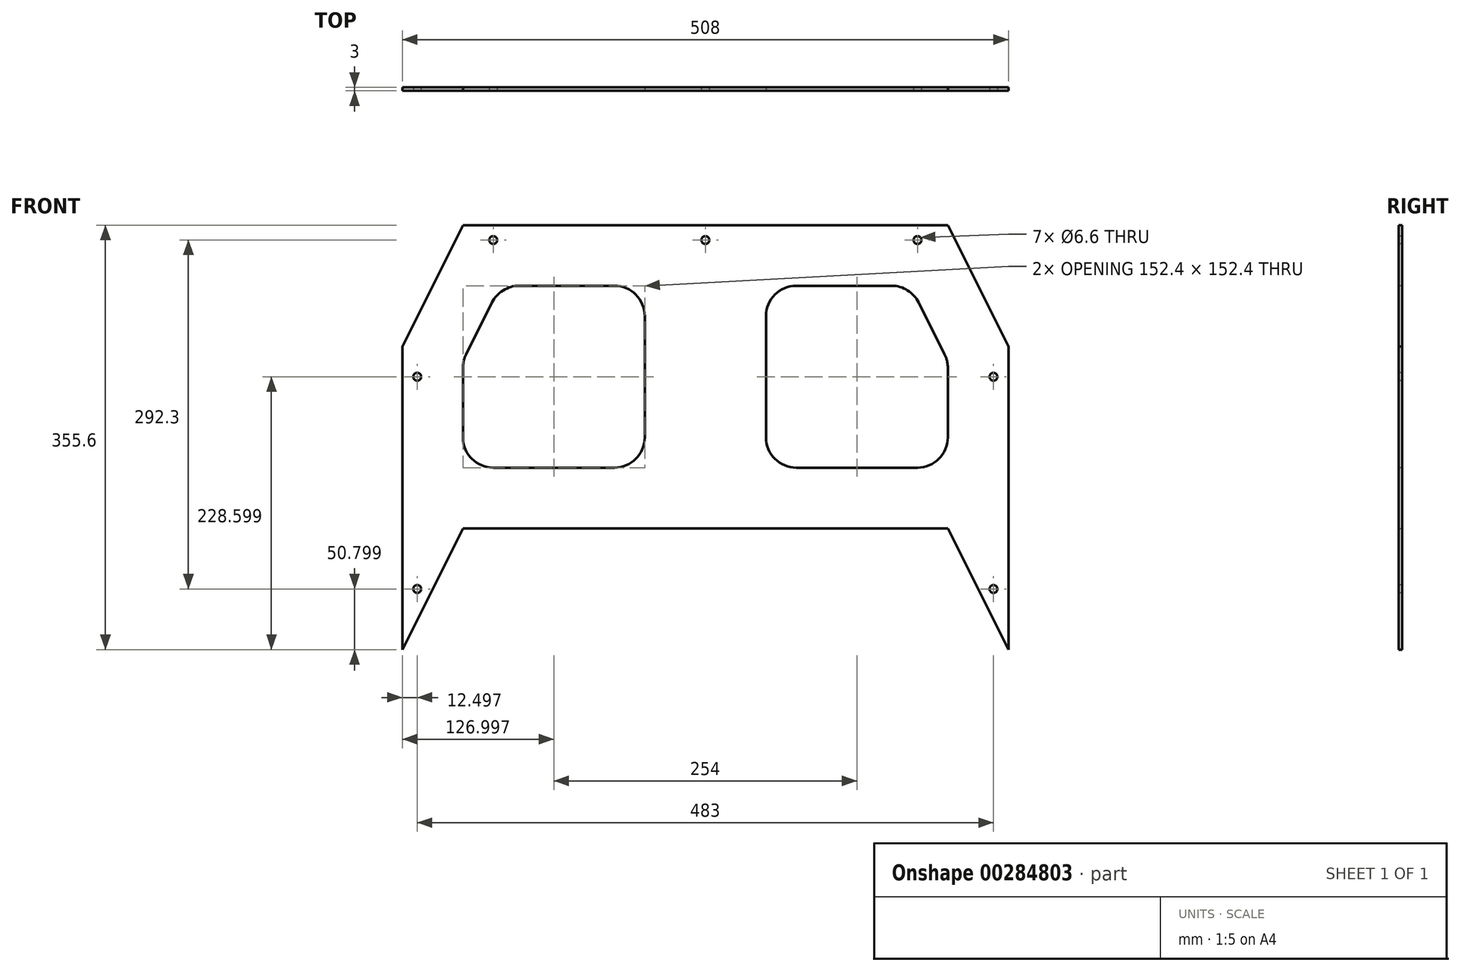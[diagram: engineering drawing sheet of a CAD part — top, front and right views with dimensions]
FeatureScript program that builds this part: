
annotation { "Feature Type Name" : "Feature", "Feature Type Description" : "" }
export const myFeature = defineFeature(function(context is Context, id is Id, definition is map)
    precondition{}
    {
        {
            var Q0;
            Q0=qCreatedBy(makeId("Front.planeOp"),FACE);
            var sketch = newSketch(context, id + "F0", { "sketchPlane" : qUnion([Q0])});
            skLineSegment(sketch, "E0", {"start": v(-249.2, -132.6) * mm, "end": v(-249.2, 121.4) * mm});
            skLineSegment(sketch, "E1", {"start": v(-249.2, 121.4) * mm, "end": v(-198.4, 223) * mm});
            skLineSegment(sketch, "E2", {"start": v(-198.4, 223) * mm, "end": v(208, 223) * mm});
            skLineSegment(sketch, "E3", {"start": v(208, 223) * mm, "end": v(258.8, 121.4) * mm});
            skLineSegment(sketch, "E4", {"start": v(258.8, 121.4) * mm, "end": v(258.8, -132.6) * mm});
            skLineSegment(sketch, "E5", {"start": v(-249.2, -132.6) * mm, "end": v(-198.4, -31) * mm});
            skLineSegment(sketch, "E6", {"start": v(-198.4, -31) * mm, "end": v(208, -31) * mm});
            skLineSegment(sketch, "E7", {"start": v(208, -31) * mm, "end": v(258.8, -132.6) * mm});
            skSolve(sketch);
        }
        {
            var Q0;
            Q0 = qSketchRegion(id + "F0", true);
            extrude(context, id + "F1", {"entities" : qUnion([Q0]), "depth" : 3 * mm});
        }
        {
            var Q0;
            Q0=makeQuery(id+"F1.opExtrude","CAP_FACE",FACE,{"disambiguationData":[OSD([sQuery(id+"F0.wireOp",EDGE,"E0"),sQuery(id+"F0.wireOp",EDGE,"E1"),sQuery(id+"F0.wireOp",EDGE,"E2"),sQuery(id+"F0.wireOp",EDGE,"E3"),sQuery(id+"F0.wireOp",EDGE,"E4"),sQuery(id+"F0.wireOp",EDGE,"E5"),sQuery(id+"F0.wireOp",EDGE,"E6"),sQuery(id+"F0.wireOp",EDGE,"E7")])],"isStart":false});
            var sketch = newSketch(context, id + "F2", { "sketchPlane" : qUnion([Q0])});
            skLineSegment(sketch, "E8", {"start": v(-173, 19.8) * mm, "end": v(-71.4, 19.8) * mm});
            skLineSegment(sketch, "E9", {"start": v(-46, 45.2) * mm, "end": v(-46, 146.8) * mm});
            skLineSegment(sketch, "E10", {"start": v(-71.4, 172.2) * mm, "end": v(-151.3, 172.2) * mm});
            skLineSegment(sketch, "E11", {"start": v(-174.02, 158.17) * mm, "end": v(-195.71, 114.78) * mm});
            skLineSegment(sketch, "E12", {"start": v(-198.4, 103.42) * mm, "end": v(-198.4, 45.2) * mm});
            skPoint(sketch, "E13.visualSharp", {"position": v(-167, 172.2) * mm});
            skArc(sketch, "E13.filletArc", {"start": v(-151.3, 172.2) * mm, "mid": v(-164.65, 168.42) * mm, "end": v(-174.02, 158.17) * mm});
            skPoint(sketch, "E14.visualSharp", {"position": v(-46, 172.2) * mm});
            skArc(sketch, "E14.filletArc", {"start": v(-46, 146.8) * mm, "mid": v(-53.43, 164.77) * mm, "end": v(-71.4, 172.2) * mm});
            skPoint(sketch, "E15.visualSharp", {"position": v(-46, 19.8) * mm});
            skArc(sketch, "E15.filletArc", {"start": v(-71.4, 19.8) * mm, "mid": v(-53.43, 27.25) * mm, "end": v(-46, 45.2) * mm});
            skPoint(sketch, "E16.visualSharp", {"position": v(-198.4, 19.8) * mm});
            skArc(sketch, "E16.filletArc", {"start": v(-198.4, 45.2) * mm, "mid": v(-190.95, 27.25) * mm, "end": v(-173, 19.8) * mm});
            skPoint(sketch, "E17.visualSharp", {"position": v(-198.4, 109.42) * mm});
            skArc(sketch, "E17.filletArc", {"start": v(-195.71, 114.78) * mm, "mid": v(-197.71, 109.26) * mm, "end": v(-198.4, 103.42) * mm});
            skArc(sketch, "E18.MirrorCS", {"start": v(205.33, 114.78) * mm, "mid": v(207.33, 109.26) * mm, "end": v(208, 103.42) * mm});
            skArc(sketch, "E19.MirrorCS", {"start": v(160.91, 172.2) * mm, "mid": v(174.27, 168.42) * mm, "end": v(183.63, 158.17) * mm});
            skLineSegment(sketch, "E20.MirrorCS", {"start": v(81, 172.2) * mm, "end": v(160.91, 172.2) * mm});
            skLineSegment(sketch, "E21.MirrorCS", {"start": v(55.6, 45.2) * mm, "end": v(55.6, 146.8) * mm});
            skLineSegment(sketch, "E22.MirrorCS", {"start": v(182.6, 19.8) * mm, "end": v(81, 19.8) * mm});
            skArc(sketch, "E23.MirrorCS", {"start": v(55.6, 146.8) * mm, "mid": v(63.05, 164.77) * mm, "end": v(81, 172.2) * mm});
            skPoint(sketch, "E24.MirrorP", {"position": v(176.61, 172.2) * mm});
            skArc(sketch, "E25.MirrorCS", {"start": v(81, 19.8) * mm, "mid": v(63.05, 27.25) * mm, "end": v(55.6, 45.2) * mm});
            skLineSegment(sketch, "E26.MirrorCS", {"start": v(183.63, 158.17) * mm, "end": v(205.33, 114.78) * mm});
            skPoint(sketch, "E27.MirrorP", {"position": v(55.6, 172.2) * mm});
            skPoint(sketch, "E28.MirrorP", {"position": v(208, 19.8) * mm});
            skPoint(sketch, "E29.MirrorP", {"position": v(55.6, 19.8) * mm});
            skArc(sketch, "E30.MirrorCS", {"start": v(208, 45.2) * mm, "mid": v(200.57, 27.25) * mm, "end": v(182.6, 19.8) * mm});
            skPoint(sketch, "E31.MirrorP", {"position": v(208, 109.42) * mm});
            skLineSegment(sketch, "E32.MirrorCS", {"start": v(208, 103.42) * mm, "end": v(208, 45.2) * mm});
            skSolve(sketch);
        }
        {
            var Q0;
            Q0 = qSketchRegion(id + "F2", true);
            extrude(context, id + "F3", {"entities" : qUnion([Q0]), "operationType" : NewBodyOperationType.REMOVE, "endBound" : BoundingType.THROUGH_ALL, "oppositeDirection" : true, "depth" : 25 * mm});
        }
        {
            var Q0;
            Q0=makeQuery(id+"F1.opExtrude","CAP_FACE",FACE,{"disambiguationData":[OSD([sQuery(id+"F0.wireOp",EDGE,"E0"),sQuery(id+"F0.wireOp",EDGE,"E1"),sQuery(id+"F0.wireOp",EDGE,"E2"),sQuery(id+"F0.wireOp",EDGE,"E3"),sQuery(id+"F0.wireOp",EDGE,"E4"),sQuery(id+"F0.wireOp",EDGE,"E5"),sQuery(id+"F0.wireOp",EDGE,"E6"),sQuery(id+"F0.wireOp",EDGE,"E7")])],"isStart":false});
            var sketch = newSketch(context, id + "F4", { "sketchPlane" : qUnion([Q0])});
            skPoint(sketch, "E33", {"position": v(-236.7, 96) * mm});
            skPoint(sketch, "E34", {"position": v(-236.7, -81.8) * mm});
            skPoint(sketch, "E35", {"position": v(-173, 210.5) * mm});
            skPoint(sketch, "E36", {"position": v(4.8, 210.5) * mm});
            skPoint(sketch, "E37", {"position": v(182.6, 210.5) * mm});
            skPoint(sketch, "E38", {"position": v(246.3, 96) * mm});
            skPoint(sketch, "E39", {"position": v(246.3, -81.8) * mm});
            skSolve(sketch);
        }
        {
            var Q0;
            Q0=sQuery(id+"F4.wireOp",VERTEX,"E35");
            var Q1;
            Q1=sQuery(id+"F4.wireOp",VERTEX,"E36");
            var Q2;
            Q2=sQuery(id+"F4.wireOp",VERTEX,"E37");
            var Q3;
            Q3=sQuery(id+"F4.wireOp",VERTEX,"E38");
            var Q4;
            Q4=sQuery(id+"F4.wireOp",VERTEX,"E39");
            var Q5;
            Q5=sQuery(id+"F4.wireOp",VERTEX,"E34");
            var Q6;
            Q6=sQuery(id+"F4.wireOp",VERTEX,"E33");
            var Q7;
            Q7=makeQuery(id+"F1.opExtrude","SWEPT_BODY",BODY,{"disambiguationData":[OSD([sQuery(id+"F0.wireOp",EDGE,"E0"),sQuery(id+"F0.wireOp",EDGE,"E1"),sQuery(id+"F0.wireOp",EDGE,"E2"),sQuery(id+"F0.wireOp",EDGE,"E3"),sQuery(id+"F0.wireOp",EDGE,"E4"),sQuery(id+"F0.wireOp",EDGE,"E5"),sQuery(id+"F0.wireOp",EDGE,"E6"),sQuery(id+"F0.wireOp",EDGE,"E7")])]});
            hole(context, id + "F5", {"style" : HoleStyle.SIMPLE, "endStyle" : HoleEndStyle.THROUGH, "standardTappedOrClearance" : lookupTablePath({ "standard" : "ISO", "fit" : "Normal", "size" : "M6", "type" : "Clearance" }), "standardBlindInLast" : lookupTablePath({ "fit" : "Standard", "standard" : "ISO", "size" : "M6", "type" : "Clearance" }), "holeDiameter" : 6.6 * mm, "tappedDepth" : 12 * mm, "tapClearance" : 3, "locations" : qUnion([Q0, Q1, Q2, Q3, Q4, Q5, Q6]), "scope" : qUnion([Q7])});
        }
    });
